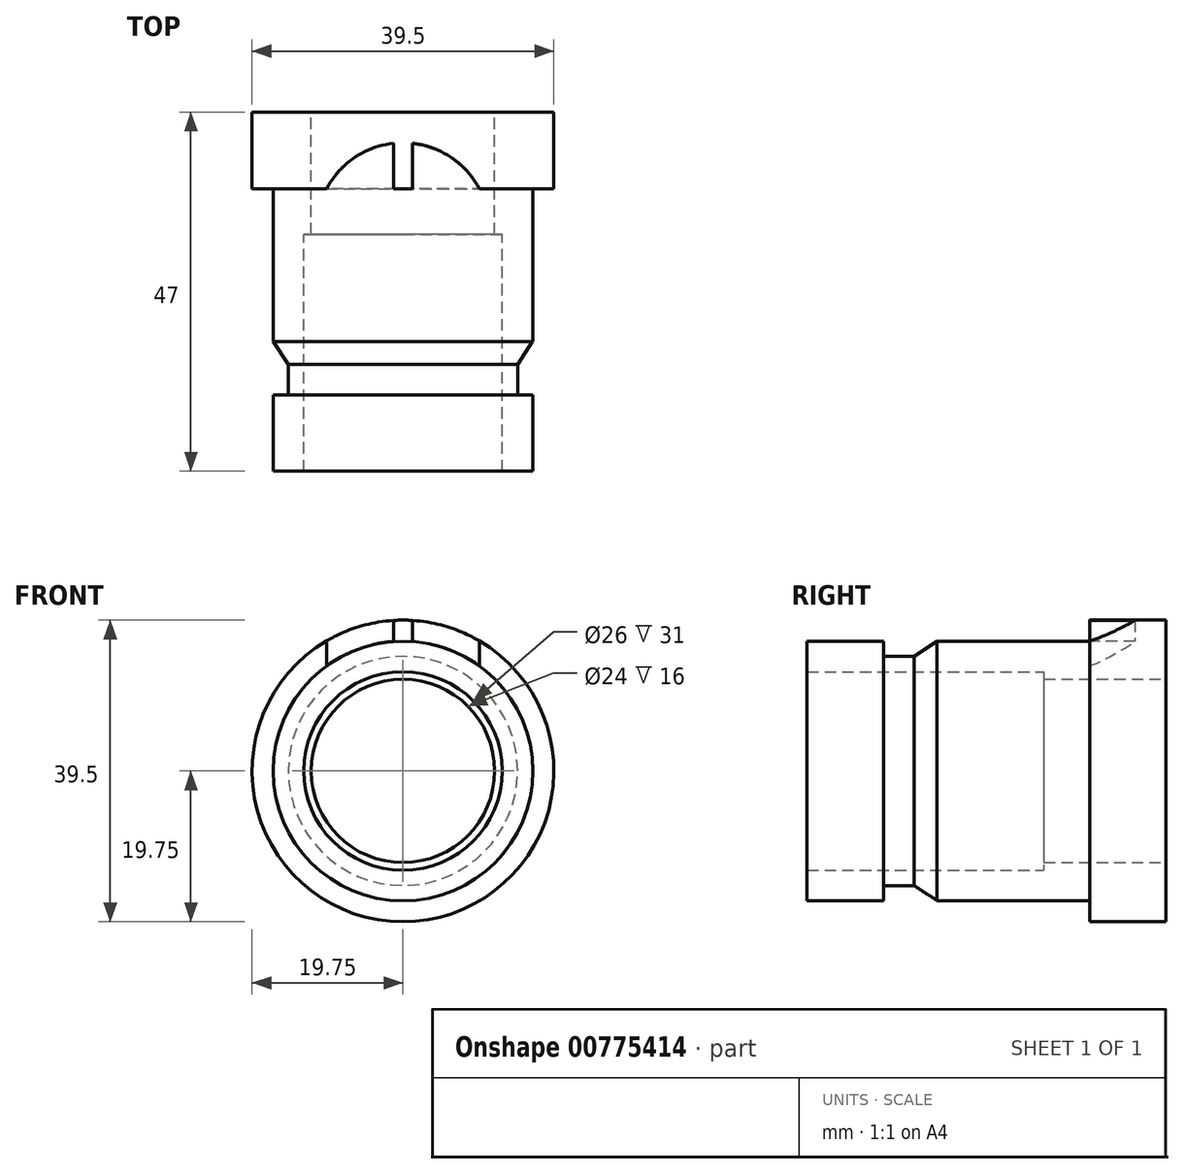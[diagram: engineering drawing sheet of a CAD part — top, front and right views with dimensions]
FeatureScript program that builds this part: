
annotation { "Feature Type Name" : "Feature", "Feature Type Description" : "" }
export const myFeature = defineFeature(function(context is Context, id is Id, definition is map)
    precondition{}
    {
        {
            var Q0;
            Q0=qCreatedBy(makeId("Front.planeOp"),FACE);
            var sketch = newSketch(context, id + "F0", { "sketchPlane" : qUnion([Q0])});
            skCircle(sketch, "E0", {"center": v(0, 0) * mm, "radius": 13 * mm});
            skCircle(sketch, "E1", {"center": v(0, 0) * mm, "radius": 17 * mm});
            skCircle(sketch, "E2", {"center": v(0, 0) * mm, "radius": 15 * mm});
            skSolve(sketch);
        }
        {
            var Q0;
            Q0=makeQuery(id+"F0.imprint","IMPRINT",FACE,{"disambiguationData":[TD([[makeQuery(id+"F0.imprint","IMPRINT",EDGE,{"derivedFrom":sQuery(id+"F0.wireOp",EDGE,"E0")}),-1.0]])]});
            var Q1;
            Q1=makeQuery(id+"F0.imprint","IMPRINT",FACE,{"disambiguationData":[TD([[makeQuery(id+"F0.imprint","IMPRINT",EDGE,{"derivedFrom":sQuery(id+"F0.wireOp",EDGE,"E1")}),1.0]])]});
            extrude(context, id + "F1", {"entities" : qUnion([Q0, Q1]), "depth" : 10 * mm, "offsetDistance" : 25 * mm});
        }
        {
            var Q0;
            Q0=makeQuery(id+"F0.imprint","IMPRINT",FACE,{"disambiguationData":[TD([[makeQuery(id+"F0.imprint","IMPRINT",EDGE,{"derivedFrom":sQuery(id+"F0.wireOp",EDGE,"E0")}),-1.0]])]});
            extrude(context, id + "F2", {"entities" : qUnion([Q0]), "operationType" : NewBodyOperationType.ADD, "oppositeDirection" : true, "depth" : 4 * mm, "offsetDistance" : 25 * mm});
        }
        {
            var Q0;
            Q0=qCreatedBy(makeId("Front.planeOp"),FACE);
            cPlane(context, id + "F3", {"entities" : qUnion([Q0]), "cplaneType" : CPlaneType.OFFSET, "offset" : 7 * mm, "oppositeDirection" : true, "width" : 150 * mm, "height" : 150 * mm});
        }
        {
            var Q0;
            Q0=qCreatedBy(id+"F3.planeOp",FACE);
            var sketch = newSketch(context, id + "F4", { "sketchPlane" : qUnion([Q0])});
            skCircle(sketch, "E3.0", {"center": v(0, 0) * mm, "radius": 17 * mm});
            skCircle(sketch, "E4.0", {"center": v(0, 0) * mm, "radius": 13 * mm});
            skSolve(sketch);
        }
        {
            var Q0;
            Q0=makeQuery(id+"F4.imprint","IMPRINT",FACE,{"disambiguationData":[TD([[makeQuery(id+"F4.imprint","IMPRINT",EDGE,{"derivedFrom":sQuery(id+"F4.wireOp",EDGE,"E3.0")}),1.0]])]});
            extrude(context, id + "F5", {"entities" : qUnion([Q0]), "oppositeDirection" : true, "depth" : 20 * mm, "offsetDistance" : 25 * mm});
        }
        {
            var Q0;
            Q0=makeQuery(id+"F2.opExtrude","CAP_FACE",FACE,{"disambiguationData":[OSD([sQuery(id+"F0.wireOp",EDGE,"E0"),sQuery(id+"F0.wireOp",EDGE,"E2")])],"isStart":false});
            var Q1;
            Q1=makeQuery(id+"F5.opExtrude","CAP_FACE",FACE,{"disambiguationData":[OSD([sQuery(id+"F4.wireOp",EDGE,"E3.0"),sQuery(id+"F4.wireOp",EDGE,"E4.0")])],"isStart":true});
            extrude(context, id + "F6", {"entities" : qUnion([Q0]), "operationType" : NewBodyOperationType.ADD, "endBound" : BoundingType.UP_TO_SURFACE, "depth" : 25 * mm, "endBoundEntityFace" : qUnion([Q1]), "offsetDistance" : 25 * mm, "hasDraft" : true, "draftAngle" : 33 * degree});
        }
        {
            var Q0;
            Q0=makeQuery(id+"F5.opExtrude","CAP_FACE",FACE,{"disambiguationData":[OSD([sQuery(id+"F4.wireOp",EDGE,"E3.0"),sQuery(id+"F4.wireOp",EDGE,"E4.0")])],"isStart":false});
            var sketch = newSketch(context, id + "F7", { "sketchPlane" : qUnion([Q0])});
            skCircle(sketch, "E5.0", {"center": v(0, 0) * mm, "radius": 13 * mm});
            skCircle(sketch, "E6", {"center": v(0, 0) * mm, "radius": 19.75 * mm});
            skSolve(sketch);
        }
        {
            var Q0;
            Q0=makeQuery(id+"F7.imprint","IMPRINT",FACE,{"disambiguationData":[TD([[makeQuery(id+"F7.imprint","IMPRINT",EDGE,{"derivedFrom":sQuery(id+"F7.wireOp",EDGE,"E6")}),1.0]])]});
            var Q1;
            Q1=makeQuery(id+"F7.imprint","IMPRINT",FACE,{"disambiguationData":[TD([[makeQuery(id+"F7.imprint","IMPRINT",EDGE,{"derivedFrom":sQuery(id+"F7.wireOp",EDGE,"E5.0")}),1.0]])]});
            extrude(context, id + "F8", {"entities" : qUnion([Q0, Q1]), "operationType" : NewBodyOperationType.ADD, "depth" : 10 * mm, "offsetDistance" : 25 * mm});
        }
        {
            var Q0;
            Q0=qCreatedBy(makeId("Top.planeOp"),FACE);
            var sketch = newSketch(context, id + "F9", { "sketchPlane" : qUnion([Q0])});
            skLineSegment(sketch, "E7", {"start": v(0, 0) * mm, "end": v(0, 27) * mm, "construction": true});
            skLineSegment(sketch, "E8.0", {"start": v(-19.75, 27) * mm, "end": v(19.75, 27) * mm});
            skPoint(sketch, "E9", {"position": v(-10, 27) * mm});
            skLineSegment(sketch, "E10", {"start": v(-1.25, 27) * mm, "end": v(-1.25, 32.93) * mm});
            skPoint(sketch, "E11.MirrorP", {"position": v(10, 27) * mm});
            skLineSegment(sketch, "E12.MirrorCS", {"start": v(1.25, 27) * mm, "end": v(1.25, 32.93) * mm});
            skPoint(sketch, "E13", {"position": v(0, 33) * mm});
            skArc(sketch, "E14", {"start": v(10, 27) * mm, "mid": v(0, 33) * mm, "end": v(-10, 27) * mm});
            skSolve(sketch);
        }
        {
            var Q0;
            {var subQ0=sQuery(id+"F9.wireOp",EDGE,"E10");Q0=makeQuery(id+"F9.imprint","IMPRINT",FACE,{"disambiguationData":[TD([[makeQuery(id+"F9.imprint","IMPRINT",EDGE,{"derivedFrom":subQ0}),1.0]])]});}
            var Q1;
            {var subQ0=sQuery(id+"F9.wireOp",EDGE,"E12.MirrorCS");Q1=makeQuery(id+"F9.imprint","IMPRINT",FACE,{"disambiguationData":[TD([[makeQuery(id+"F9.imprint","IMPRINT",EDGE,{"derivedFrom":subQ0}),-1.0]])]});}
            extrude(context, id + "F10", {"entities" : qUnion([Q0, Q1]), "operationType" : NewBodyOperationType.REMOVE, "endBound" : BoundingType.THROUGH_ALL, "depth" : 25 * mm, "offsetDistance" : 25 * mm});
        }
        {
            var Q0;
            {var subQ0=sQuery(id+"F9.wireOp",EDGE,"E8.0");Q0=makeQuery(id+"F10.boolean.opBoolean","COPY",FACE,{"derivedFrom":makeQuery(id+"F10.opExtrude","SWEPT_FACE",FACE,{"disambiguationData":[OSD([subQ0]),TDD([makeQuery(id+"F9.imprint","IMPRINT",EDGE,{"disambiguationData":[TD([[makeQuery(id+"F9.imprint","INTERSECT",VERTEX,{"derivedFrom":[subQ0,sQuery(id+"F9.wireOp",EDGE,"E10")]}),1.0]])],"derivedFrom":subQ0})])]})});}
            var Q1;
            {var subQ0=sQuery(id+"F9.wireOp",EDGE,"E8.0");Q1=makeQuery(id+"F10.boolean.opBoolean","COPY",FACE,{"derivedFrom":makeQuery(id+"F10.opExtrude","SWEPT_FACE",FACE,{"disambiguationData":[OSD([subQ0]),TDD([makeQuery(id+"F9.imprint","IMPRINT",EDGE,{"disambiguationData":[TD([[makeQuery(id+"F9.imprint","INTERSECT",VERTEX,{"derivedFrom":[subQ0,sQuery(id+"F9.wireOp",EDGE,"E12.MirrorCS")]}),-1.0]])],"derivedFrom":subQ0})])]})});}
            var Q2;
            Q2=makeQuery(id+"F8.opExtrude","CAP_FACE",FACE,{"disambiguationData":[OSD([sQuery(id+"F7.wireOp",EDGE,"E5.0"),sQuery(id+"F7.wireOp",EDGE,"E6")])],"isStart":false});
            extrude(context, id + "F11", {"entities" : qUnion([Q0, Q1]), "operationType" : NewBodyOperationType.ADD, "endBound" : BoundingType.UP_TO_SURFACE, "depth" : 25 * mm, "endBoundEntityFace" : qUnion([Q2]), "offsetDistance" : 25 * mm});
        }
        {
            var Q0;
            Q0=makeQuery(id+"F8.opExtrude","CAP_FACE",FACE,{"disambiguationData":[OSD([sQuery(id+"F7.wireOp",EDGE,"E5.0"),sQuery(id+"F7.wireOp",EDGE,"E6")])],"isStart":false});
            var sketch = newSketch(context, id + "F12", { "sketchPlane" : qUnion([Q0])});
            skPoint(sketch, "E15.0", {"position": v(0, 0) * mm});
            skCircle(sketch, "E16", {"center": v(0, 0) * mm, "radius": 12 * mm});
            skCircle(sketch, "E17", {"center": v(0, 0) * mm, "radius": 13 * mm});
            skSolve(sketch);
        }
        {
            var Q0;
            Q0=makeQuery(id+"F12.imprint","IMPRINT",FACE,{"disambiguationData":[TD([[makeQuery(id+"F12.imprint","IMPRINT",EDGE,{"derivedFrom":sQuery(id+"F12.wireOp",EDGE,"E16")}),-1.0]])]});
            extrude(context, id + "F13", {"entities" : qUnion([Q0]), "operationType" : NewBodyOperationType.ADD, "oppositeDirection" : true, "depth" : 16 * mm, "offsetDistance" : 25 * mm});
        }
        {
            var Q0;
            Q0=makeQuery(id+"F1.opExtrude","CAP_FACE",FACE,{"disambiguationData":[OSD([sQuery(id+"F0.wireOp",EDGE,"E0"),sQuery(id+"F0.wireOp",EDGE,"E1")])],"isStart":false});
            var sketch = newSketch(context, id + "F14", { "sketchPlane" : qUnion([Q0])});
            skCircle(sketch, "E18.0", {"center": v(0, 0) * mm, "radius": 13 * mm});
            skSolve(sketch);
        }
        {
            var Q0;
            Q0=makeQuery(id+"F14.imprint","IMPRINT",FACE,{"disambiguationData":[TD([[makeQuery(id+"F14.imprint","IMPRINT",EDGE,{"derivedFrom":sQuery(id+"F14.wireOp",EDGE,"E18.0")}),1.0]])]});
            var Q1;
            Q1=makeQuery(id+"F13.opExtrude","CAP_FACE",FACE,{"disambiguationData":[OSD([sQuery(id+"F12.wireOp",EDGE,"E16"),sQuery(id+"F12.wireOp",EDGE,"E17")])],"isStart":false});
            extrude(context, id + "F15", {"entities" : qUnion([Q0]), "operationType" : NewBodyOperationType.REMOVE, "endBound" : BoundingType.UP_TO_SURFACE, "oppositeDirection" : true, "depth" : 25 * mm, "endBoundEntityFace" : qUnion([Q1]), "offsetDistance" : 25 * mm});
        }
    });
